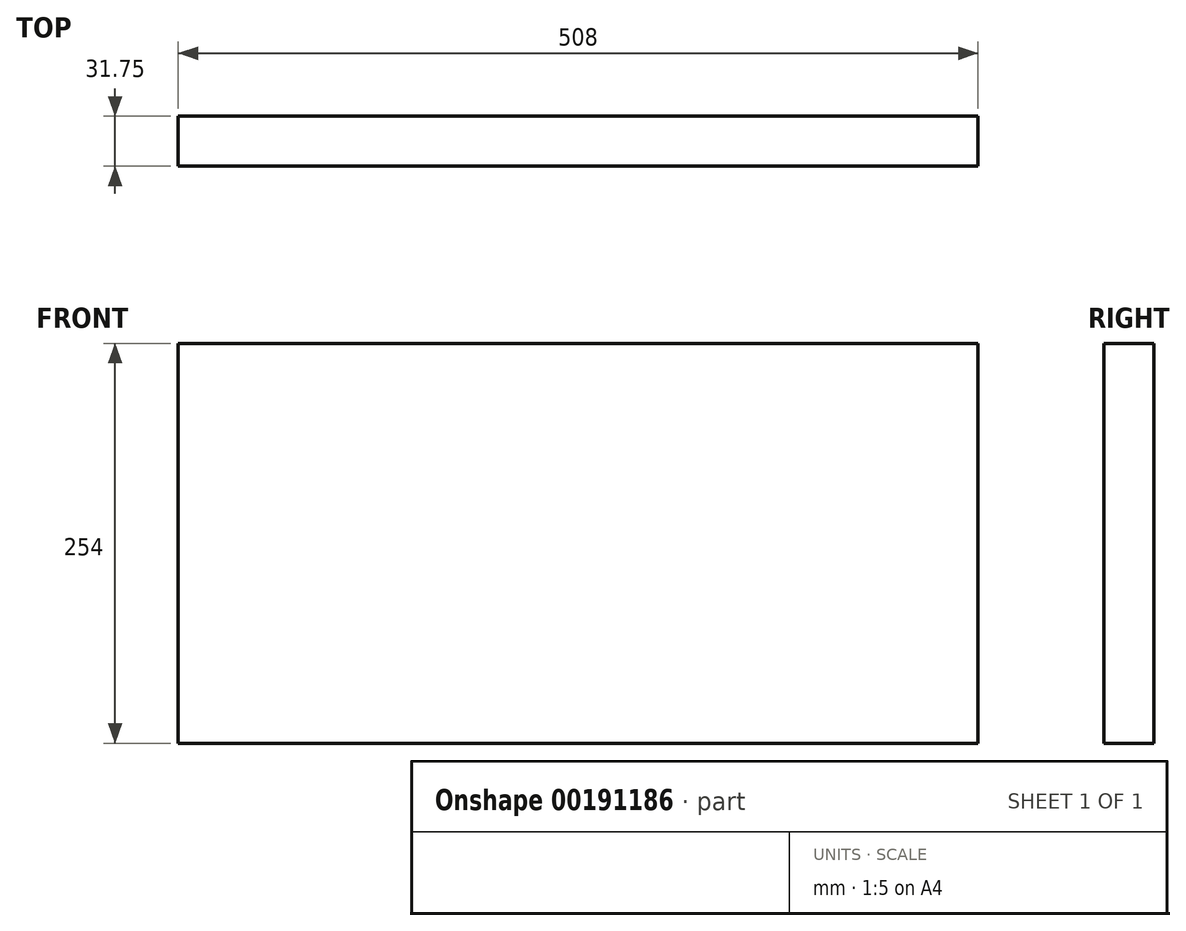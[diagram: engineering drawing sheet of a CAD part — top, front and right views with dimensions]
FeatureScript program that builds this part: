
annotation { "Feature Type Name" : "Feature", "Feature Type Description" : "" }
export const myFeature = defineFeature(function(context is Context, id is Id, definition is map)
    precondition{}
    {
        {
            var Q0;
            Q0=qCreatedBy(makeId("Front.planeOp"),FACE);
            var sketch = newSketch(context, id + "F0", { "sketchPlane" : qUnion([Q0])});
            skLineSegment(sketch, "E0.bottom", {"start": v(254, -127) * mm, "end": v(-254, -127) * mm});
            skLineSegment(sketch, "E0.top", {"start": v(254, 127) * mm, "end": v(-254, 127) * mm});
            skLineSegment(sketch, "E0.left", {"start": v(254, -127) * mm, "end": v(254, 127) * mm});
            skLineSegment(sketch, "E0.right", {"start": v(-254, -127) * mm, "end": v(-254, 127) * mm});
            skPoint(sketch, "E0.middle", {"position": v(0, 0) * mm});
            skSolve(sketch);
        }
        {
            var Q0;
            Q0 = qSketchRegion(id + "F0", true);
            extrude(context, id + "F1", {"entities" : qUnion([Q0]), "depth" : 31.75 * mm});
        }
    });
